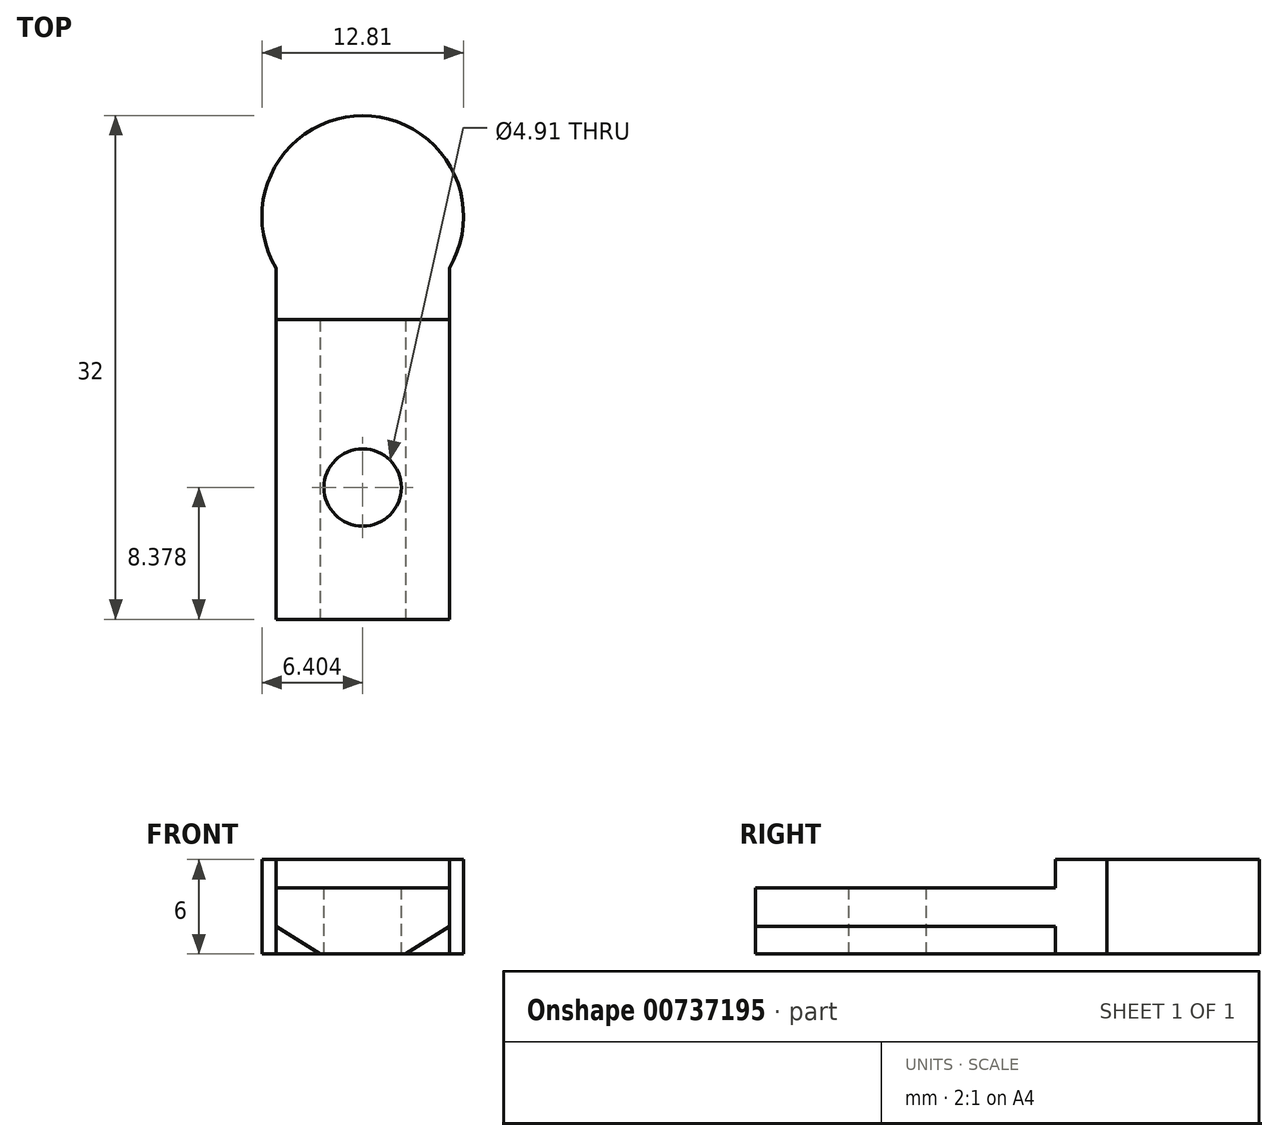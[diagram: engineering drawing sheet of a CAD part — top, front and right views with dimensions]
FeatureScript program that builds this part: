
annotation { "Feature Type Name" : "Feature", "Feature Type Description" : "" }
export const myFeature = defineFeature(function(context is Context, id is Id, definition is map)
    precondition{}
    {
        {
            var Q0;
            Q0=qCreatedBy(makeId("Top.planeOp"),FACE);
            var sketch = newSketch(context, id + "F0", { "sketchPlane" : qUnion([Q0])});
            skLineSegment(sketch, "E0.bottom", {"start": v(6.3, -11.13) * mm, "end": v(-4.71, -11.13) * mm});
            skLineSegment(sketch, "E0.top", {"start": v(6.3, 11.2) * mm, "end": v(-4.71, 11.2) * mm});
            skLineSegment(sketch, "E0.left", {"start": v(6.3, -11.13) * mm, "end": v(6.3, 11.2) * mm});
            skLineSegment(sketch, "E0.right", {"start": v(-4.71, -11.13) * mm, "end": v(-4.71, 11.2) * mm});
            skPoint(sketch, "E0.middle", {"position": v(0.8, 0.03) * mm});
            skArc(sketch, "E1", {"start": v(6.3, 11.2) * mm, "mid": v(0.8, 20.87) * mm, "end": v(-4.71, 11.2) * mm});
            skSolve(sketch);
        }
        {
            var Q0;
            Q0 = qSketchRegion(id + "F0", true);
            extrude(context, id + "F1", {"entities" : qUnion([Q0]), "depth" : 4.2 * mm + 1.8 * mm, "offsetDistance" : 25.4 * mm});
        }
        {
            var Q0;
            Q0=makeQuery(id+"F1.opExtrude","CAP_FACE",FACE,{"disambiguationData":[OSD([sQuery(id+"F0.wireOp",EDGE,"E0.bottom"),sQuery(id+"F0.wireOp",EDGE,"E0.left"),sQuery(id+"F0.wireOp",EDGE,"E0.right"),sQuery(id+"F0.wireOp",EDGE,"E1")])],"isStart":false});
            var sketch = newSketch(context, id + "F2", { "sketchPlane" : qUnion([Q0])});
            skLineSegment(sketch, "E2", {"start": v(0.8, -11.13) * mm, "end": v(0.8, 20.87) * mm});
            skCircle(sketch, "E3", {"center": v(0.8, -2.75) * mm, "radius": 2.46 * mm});
            skSolve(sketch);
        }
        {
            var Q0;
            Q0 = qSketchRegion(id + "F2", true);
            extrude(context, id + "F3", {"entities" : qUnion([Q0]), "operationType" : NewBodyOperationType.REMOVE, "endBound" : BoundingType.UP_TO_NEXT, "oppositeDirection" : true, "depth" : 25.4 * mm, "offsetDistance" : 25.4 * mm});
        }
        {
            var Q0;
            Q0=makeQuery(id+"F1.opExtrude","SWEPT_FACE",FACE,{"disambiguationData":[OSD([sQuery(id+"F0.wireOp",EDGE,"E0.bottom")])]});
            var sketch = newSketch(context, id + "F4", { "sketchPlane" : qUnion([Q0])});
            skLineSegment(sketch, "E4", {"start": v(-4.71, 1.76) * mm, "end": v(-1.92, 0) * mm});
            skLineSegment(sketch, "E5", {"start": v(-1.92, 0) * mm, "end": v(-4.71, 0) * mm});
            skLineSegment(sketch, "E6", {"start": v(-4.71, 0) * mm, "end": v(-4.71, 1.76) * mm});
            skLineSegment(sketch, "E7", {"start": v(6.3, 1.76) * mm, "end": v(3.5, 0) * mm});
            skLineSegment(sketch, "E8", {"start": v(3.5, 0) * mm, "end": v(6.3, 0) * mm});
            skLineSegment(sketch, "E9", {"start": v(6.3, 0) * mm, "end": v(6.3, 1.76) * mm});
            skLineSegment(sketch, "E10", {"start": v(0.8, 0) * mm, "end": v(0.8, 6) * mm});
            skLineSegment(sketch, "E11.bottom", {"start": v(-4.71, 6) * mm, "end": v(6.3, 6) * mm});
            skLineSegment(sketch, "E11.top", {"start": v(-4.71, 4.2) * mm, "end": v(6.3, 4.2) * mm});
            skLineSegment(sketch, "E11.left", {"start": v(-4.71, 6) * mm, "end": v(-4.71, 4.2) * mm});
            skLineSegment(sketch, "E11.right", {"start": v(6.3, 6) * mm, "end": v(6.3, 4.2) * mm});
            skSolve(sketch);
        }
        {
            var Q0;
            Q0 = qSketchRegion(id + "F4", true);
            extrude(context, id + "F5", {"entities" : qUnion([Q0]), "operationType" : NewBodyOperationType.REMOVE, "oppositeDirection" : true, "depth" : 19.05 * mm, "offsetDistance" : 25.4 * mm});
        }
        {
            var Q0;
            Q0 = qSketchRegion(id + "F4", true);
            extrude(context, id + "F6", {"entities" : qUnion([Q0]), "operationType" : NewBodyOperationType.REMOVE, "oppositeDirection" : true, "depth" : 19.05 * mm, "offsetDistance" : 25.4 * mm});
        }
    });
